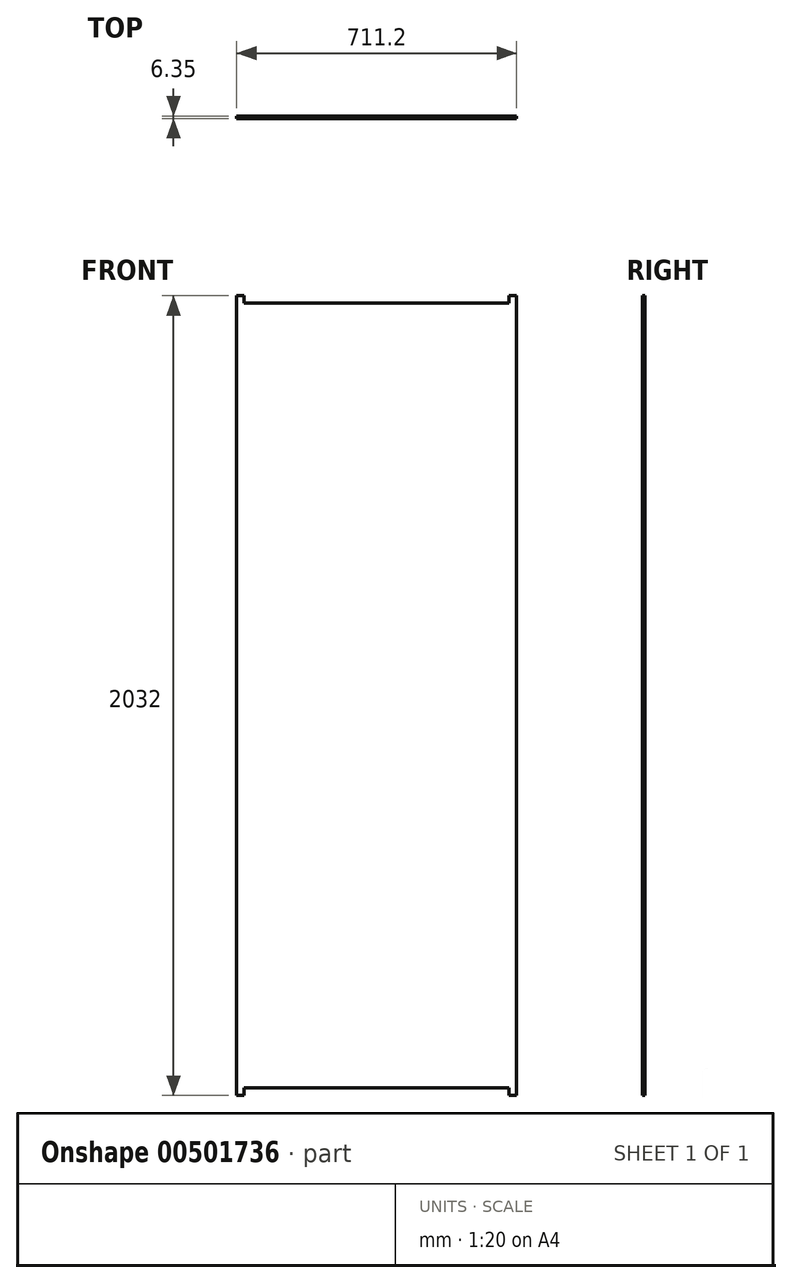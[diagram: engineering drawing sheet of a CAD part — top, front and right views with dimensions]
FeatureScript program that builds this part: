
annotation { "Feature Type Name" : "Feature", "Feature Type Description" : "" }
export const myFeature = defineFeature(function(context is Context, id is Id, definition is map)
    precondition{}
    {
        {
            var Q0;
            Q0=qCreatedBy(makeId("Front.planeOp"),FACE);
            var sketch = newSketch(context, id + "F0", { "sketchPlane" : qUnion([Q0])});
            skLineSegment(sketch, "E0.bottom", {"start": v(-355.6, 1016) * mm, "end": v(355.6, 1016) * mm});
            skLineSegment(sketch, "E0.top", {"start": v(-355.6, -1016) * mm, "end": v(355.6, -1016) * mm});
            skLineSegment(sketch, "E0.left", {"start": v(-355.6, 1016) * mm, "end": v(-355.6, -1016) * mm});
            skLineSegment(sketch, "E0.right", {"start": v(355.6, 1016) * mm, "end": v(355.6, -1016) * mm});
            skPoint(sketch, "E0.middle", {"position": v(0, 0) * mm});
            skLineSegment(sketch, "E1", {"start": v(-336.55, 1016) * mm, "end": v(-336.55, 996.95) * mm});
            skLineSegment(sketch, "E2", {"start": v(-336.55, 996.95) * mm, "end": v(336.55, 996.95) * mm});
            skLineSegment(sketch, "E3", {"start": v(336.55, 996.95) * mm, "end": v(336.55, 1016) * mm});
            skLineSegment(sketch, "E4", {"start": v(-336.55, -1016) * mm, "end": v(-336.55, -996.95) * mm});
            skLineSegment(sketch, "E5", {"start": v(-336.55, -996.95) * mm, "end": v(336.55, -996.95) * mm});
            skLineSegment(sketch, "E6", {"start": v(336.55, -996.95) * mm, "end": v(336.55, -1016) * mm});
            skSolve(sketch);
        }
        {
            var Q0;
            Q0=makeQuery(id+"F0.imprint","IMPRINT",FACE,{"disambiguationData":[TD([[makeQuery(id+"F0.imprint","IMPRINT",EDGE,{"derivedFrom":sQuery(id+"F0.wireOp",EDGE,"E0.bottom")}),-1.0]])]});
            extrude(context, id + "F1", {"entities" : qUnion([Q0]), "depth" : 6.35 * mm});
        }
    });
